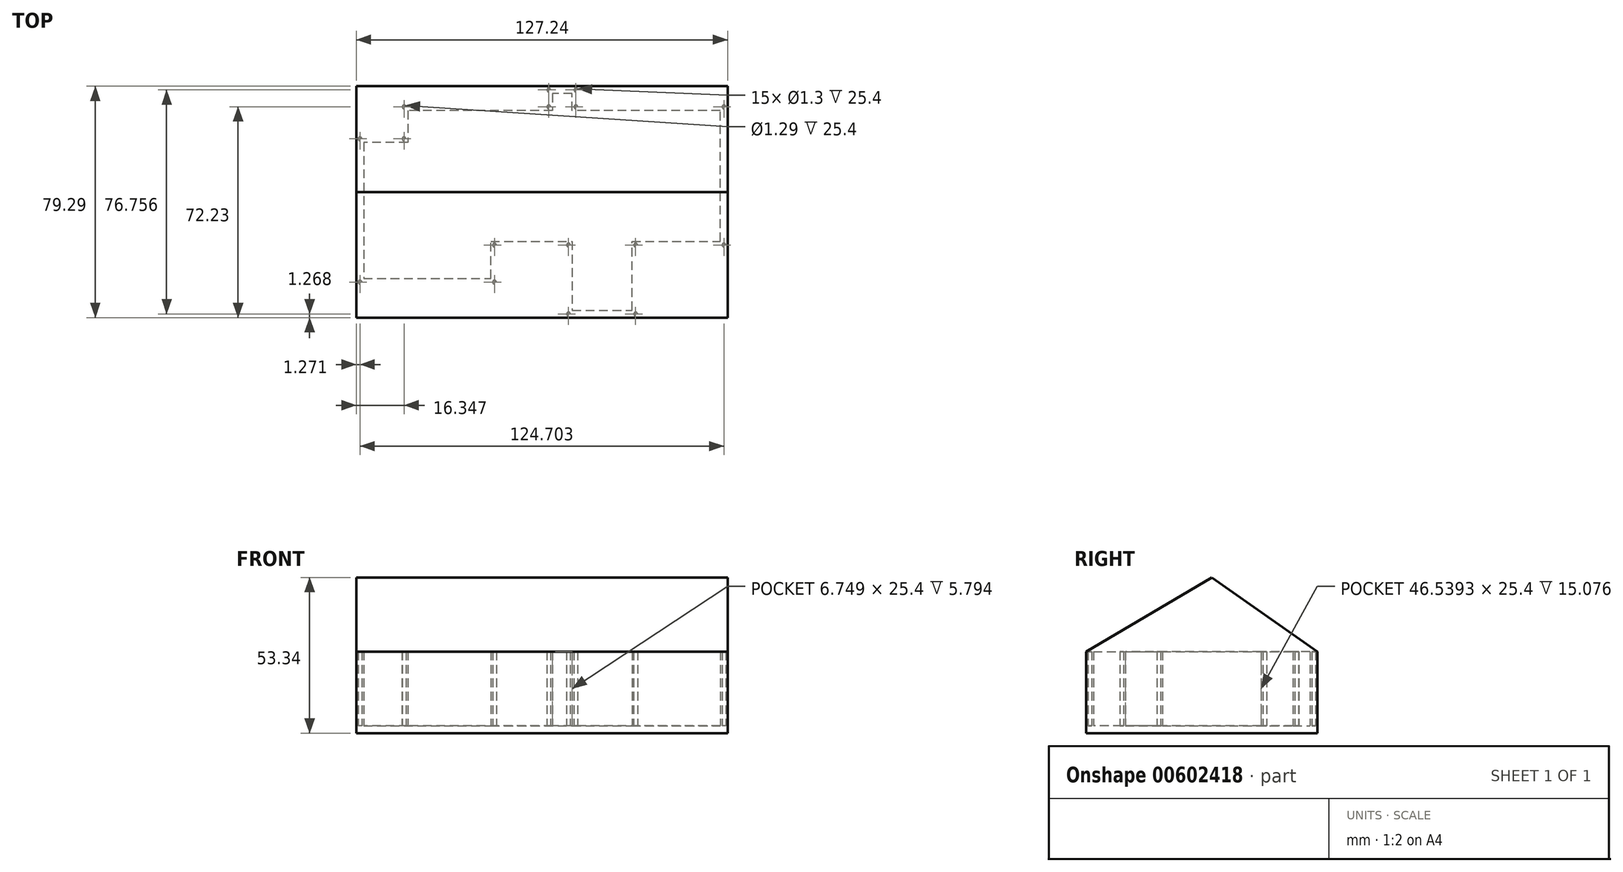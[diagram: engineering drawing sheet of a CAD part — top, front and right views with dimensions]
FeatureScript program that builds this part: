
annotation { "Feature Type Name" : "Feature", "Feature Type Description" : "" }
export const myFeature = defineFeature(function(context is Context, id is Id, definition is map)
    precondition{}
    {
        {
            var Q0;
            Q0=qCreatedBy(makeId("Top.planeOp"),FACE);
            var sketch = newSketch(context, id + "F0", { "sketchPlane" : qUnion([Q0])});
            skLineSegment(sketch, "E0", {"start": v(-47.22, 30.42) * mm, "end": v(2.39, 30.42) * mm});
            skLineSegment(sketch, "E1", {"start": v(2.39, 30.42) * mm, "end": v(2.39, 36.21) * mm});
            skLineSegment(sketch, "E2", {"start": v(2.39, 36.21) * mm, "end": v(14.22, 36.21) * mm});
            skLineSegment(sketch, "E3", {"start": v(14.22, 36.21) * mm, "end": v(14.22, 30.42) * mm});
            skLineSegment(sketch, "E4", {"start": v(14.22, 30.42) * mm, "end": v(64.94, 30.42) * mm});
            skLineSegment(sketch, "E5", {"start": v(-47.22, 30.42) * mm, "end": v(-47.22, 19.46) * mm});
            skLineSegment(sketch, "E6", {"start": v(-47.22, 19.46) * mm, "end": v(-62.3, 19.46) * mm});
            skLineSegment(sketch, "E7", {"start": v(-62.3, 19.46) * mm, "end": v(-62.3, -32.16) * mm});
            skLineSegment(sketch, "E8", {"start": v(-62.3, -32.16) * mm, "end": v(-13.68, -32.16) * mm});
            skLineSegment(sketch, "E9", {"start": v(-13.68, -32.16) * mm, "end": v(-13.68, -19.46) * mm});
            skLineSegment(sketch, "E10", {"start": v(-13.68, -19.46) * mm, "end": v(9.14, -19.46) * mm});
            skLineSegment(sketch, "E11", {"start": v(9.14, -19.46) * mm, "end": v(9.14, -43.08) * mm});
            skLineSegment(sketch, "E12", {"start": v(9.14, -43.08) * mm, "end": v(34.68, -43.08) * mm});
            skLineSegment(sketch, "E13", {"start": v(34.68, -43.08) * mm, "end": v(34.68, -19.46) * mm});
            skLineSegment(sketch, "E14", {"start": v(34.68, -19.46) * mm, "end": v(64.94, -19.46) * mm});
            skLineSegment(sketch, "E15", {"start": v(64.94, -19.46) * mm, "end": v(64.94, 30.42) * mm});
            skLineSegment(sketch, "E16", {"start": v(11.68, -19.46) * mm, "end": v(11.68, -40.54) * mm});
            skLineSegment(sketch, "E17", {"start": v(11.68, -40.54) * mm, "end": v(32.14, -40.54) * mm});
            skLineSegment(sketch, "E18", {"start": v(32.14, -40.54) * mm, "end": v(32.14, -16.92) * mm});
            skLineSegment(sketch, "E19", {"start": v(32.14, -16.92) * mm, "end": v(62.4, -16.92) * mm});
            skLineSegment(sketch, "E20", {"start": v(62.4, -16.92) * mm, "end": v(62.4, 27.88) * mm});
            skLineSegment(sketch, "E21", {"start": v(62.4, 27.88) * mm, "end": v(11.68, 27.88) * mm});
            skLineSegment(sketch, "E22", {"start": v(11.68, 27.88) * mm, "end": v(11.68, 33.67) * mm});
            skLineSegment(sketch, "E23", {"start": v(11.68, 33.67) * mm, "end": v(4.93, 33.67) * mm});
            skLineSegment(sketch, "E24", {"start": v(4.93, 33.67) * mm, "end": v(4.93, 27.88) * mm});
            skLineSegment(sketch, "E25", {"start": v(4.93, 27.88) * mm, "end": v(-44.68, 27.88) * mm});
            skLineSegment(sketch, "E26", {"start": v(-44.68, 27.88) * mm, "end": v(-44.68, 16.92) * mm});
            skLineSegment(sketch, "E27", {"start": v(-44.68, 16.92) * mm, "end": v(-59.76, 16.92) * mm});
            skLineSegment(sketch, "E28", {"start": v(-59.76, 16.92) * mm, "end": v(-59.76, -29.62) * mm});
            skLineSegment(sketch, "E29", {"start": v(-59.76, -29.62) * mm, "end": v(-16.22, -29.62) * mm});
            skLineSegment(sketch, "E30", {"start": v(-16.22, -29.62) * mm, "end": v(-16.22, -16.92) * mm});
            skLineSegment(sketch, "E31", {"start": v(-16.22, -16.92) * mm, "end": v(11.68, -16.92) * mm});
            skLineSegment(sketch, "E32", {"start": v(11.68, -16.92) * mm, "end": v(11.68, -19.46) * mm});
            skLineSegment(sketch, "E33", {"start": v(-59.76, 1.4) * mm, "end": v(62.4, 1.4) * mm});
            skLineSegment(sketch, "E34", {"start": v(-59.76, 2.66) * mm, "end": v(62.4, 2.66) * mm});
            skLineSegment(sketch, "E35", {"start": v(-44.68, 16.92) * mm, "end": v(-44.68, 2.66) * mm});
            skLineSegment(sketch, "E36", {"start": v(-45.95, 16.92) * mm, "end": v(-45.95, 2.66) * mm});
            skLineSegment(sketch, "E37.top", {"start": v(32.14, -43.08) * mm, "end": v(34.68, -43.08) * mm});
            skLineSegment(sketch, "E37.right", {"start": v(34.68, -40.54) * mm, "end": v(34.68, -43.08) * mm});
            skLineSegment(sketch, "E38.top", {"start": v(62.4, 30.42) * mm, "end": v(64.94, 30.42) * mm});
            skLineSegment(sketch, "E38.right", {"start": v(64.94, 27.88) * mm, "end": v(64.94, 30.42) * mm});
            skLineSegment(sketch, "E39.top", {"start": v(-44.68, 30.42) * mm, "end": v(-47.22, 30.42) * mm});
            skLineSegment(sketch, "E39.right", {"start": v(-47.22, 27.88) * mm, "end": v(-47.22, 30.42) * mm});
            skLineSegment(sketch, "E40.bottom", {"start": v(-62.3, -32.16) * mm, "end": v(-59.76, -32.16) * mm});
            skLineSegment(sketch, "E40.left", {"start": v(-62.3, -32.16) * mm, "end": v(-62.3, -29.62) * mm});
            skLineSegment(sketch, "E41.top", {"start": v(-59.76, 19.46) * mm, "end": v(-62.3, 19.46) * mm});
            skLineSegment(sketch, "E41.right", {"start": v(-62.3, 16.92) * mm, "end": v(-62.3, 19.46) * mm});
            skLineSegment(sketch, "E42.top", {"start": v(62.4, -19.46) * mm, "end": v(64.94, -19.46) * mm});
            skLineSegment(sketch, "E42.right", {"start": v(64.94, -16.92) * mm, "end": v(64.94, -19.46) * mm});
            skLineSegment(sketch, "E43.top", {"start": v(34.68, -16.92) * mm, "end": v(32.14, -16.92) * mm});
            skLineSegment(sketch, "E43.right", {"start": v(32.14, -19.46) * mm, "end": v(32.14, -16.92) * mm});
            skLineSegment(sketch, "E44.bottom", {"start": v(9.14, -43.08) * mm, "end": v(11.68, -43.08) * mm});
            skLineSegment(sketch, "E44.left", {"start": v(9.14, -43.08) * mm, "end": v(9.14, -40.54) * mm});
            skLineSegment(sketch, "E45.top", {"start": v(9.14, -16.92) * mm, "end": v(11.68, -16.92) * mm});
            skLineSegment(sketch, "E45.right", {"start": v(11.68, -19.46) * mm, "end": v(11.68, -16.92) * mm});
            skLineSegment(sketch, "E46.top", {"start": v(-13.68, -16.92) * mm, "end": v(-16.22, -16.92) * mm});
            skLineSegment(sketch, "E46.right", {"start": v(-16.22, -19.46) * mm, "end": v(-16.22, -16.92) * mm});
            skLineSegment(sketch, "E47.bottom", {"start": v(14.22, 36.21) * mm, "end": v(11.68, 36.21) * mm});
            skLineSegment(sketch, "E47.left", {"start": v(14.22, 36.21) * mm, "end": v(14.22, 33.67) * mm});
            skLineSegment(sketch, "E48.bottom", {"start": v(2.39, 36.21) * mm, "end": v(4.93, 36.21) * mm});
            skLineSegment(sketch, "E48.left", {"start": v(2.39, 36.21) * mm, "end": v(2.39, 33.67) * mm});
            skLineSegment(sketch, "E49.top", {"start": v(2.39, 27.88) * mm, "end": v(4.93, 27.88) * mm});
            skLineSegment(sketch, "E49.right", {"start": v(4.93, 30.42) * mm, "end": v(4.93, 27.88) * mm});
            skLineSegment(sketch, "E50.bottom", {"start": v(11.68, 27.88) * mm, "end": v(14.22, 27.88) * mm});
            skLineSegment(sketch, "E50.left", {"start": v(11.68, 27.88) * mm, "end": v(11.68, 30.42) * mm});
            skLineSegment(sketch, "E51.bottom", {"start": v(-13.68, -32.16) * mm, "end": v(-16.22, -32.16) * mm});
            skLineSegment(sketch, "E51.left", {"start": v(-13.68, -32.16) * mm, "end": v(-13.68, -29.62) * mm});
            skLineSegment(sketch, "E52.top", {"start": v(-47.22, 16.92) * mm, "end": v(-44.68, 16.92) * mm});
            skLineSegment(sketch, "E52.right", {"start": v(-44.68, 19.46) * mm, "end": v(-44.68, 16.92) * mm});
            skCircle(sketch, "E53", {"center": v(-61.03, 18.2) * mm, "radius": 0.65 * mm});
            skPoint(sketch, "E53.centerSnap0", {"position": v(-62.3, 18.2) * mm});
            skPoint(sketch, "E53.centerSnap1", {"position": v(-61.03, 16.92) * mm});
            skCircle(sketch, "E54", {"center": v(-45.95, 29.15) * mm, "radius": 0.64 * mm});
            skPoint(sketch, "E54.centerSnap0", {"position": v(-45.95, 27.88) * mm});
            skPoint(sketch, "E54.centerSnap1", {"position": v(-47.22, 29.15) * mm});
            skCircle(sketch, "E55", {"center": v(-45.95, 18.2) * mm, "radius": 0.65 * mm});
            skPoint(sketch, "E55.centerSnap0", {"position": v(-47.22, 18.2) * mm});
            skCircle(sketch, "E56", {"center": v(-61.03, -30.89) * mm, "radius": 0.65 * mm});
            skPoint(sketch, "E56.centerSnap0", {"position": v(-61.03, -32.16) * mm});
            skPoint(sketch, "E56.centerSnap1", {"position": v(-59.76, -30.89) * mm});
            skCircle(sketch, "E57", {"center": v(-14.95, -30.89) * mm, "radius": 0.65 * mm});
            skPoint(sketch, "E57.centerSnap0", {"position": v(-14.95, -32.16) * mm});
            skPoint(sketch, "E57.centerSnap1", {"position": v(-13.68, -30.89) * mm});
            skCircle(sketch, "E58", {"center": v(-14.95, -18.19) * mm, "radius": 0.65 * mm});
            skPoint(sketch, "E58.centerSnap0", {"position": v(-16.22, -18.19) * mm});
            skPoint(sketch, "E58.centerSnap1", {"position": v(-14.95, -19.46) * mm});
            skCircle(sketch, "E59", {"center": v(10.4, -18.19) * mm, "radius": 0.65 * mm});
            skPoint(sketch, "E59.centerSnap0", {"position": v(10.4, -19.46) * mm});
            skPoint(sketch, "E59.centerSnap1", {"position": v(11.68, -18.19) * mm});
            skCircle(sketch, "E60", {"center": v(10.4, -41.81) * mm, "radius": 0.65 * mm});
            skPoint(sketch, "E60.centerSnap0", {"position": v(10.4, -43.08) * mm});
            skPoint(sketch, "E60.centerSnap1", {"position": v(9.14, -41.81) * mm});
            skCircle(sketch, "E61", {"center": v(33.41, -41.81) * mm, "radius": 0.65 * mm});
            skPoint(sketch, "E61.centerSnap0", {"position": v(33.41, -43.08) * mm});
            skPoint(sketch, "E61.centerSnap1", {"position": v(32.14, -41.81) * mm});
            skCircle(sketch, "E62", {"center": v(33.41, -18.19) * mm, "radius": 0.65 * mm});
            skPoint(sketch, "E62.centerSnap0", {"position": v(33.41, -19.46) * mm});
            skPoint(sketch, "E62.centerSnap1", {"position": v(32.14, -18.19) * mm});
            skCircle(sketch, "E63", {"center": v(63.67, -18.19) * mm, "radius": 0.65 * mm});
            skPoint(sketch, "E63.centerSnap0", {"position": v(62.4, -18.19) * mm});
            skPoint(sketch, "E63.centerSnap1", {"position": v(63.67, -19.46) * mm});
            skCircle(sketch, "E64", {"center": v(63.67, 29.15) * mm, "radius": 0.65 * mm});
            skPoint(sketch, "E64.centerSnap0", {"position": v(63.67, 27.88) * mm});
            skPoint(sketch, "E64.centerSnap1", {"position": v(64.94, 29.15) * mm});
            skCircle(sketch, "E65", {"center": v(12.95, 29.15) * mm, "radius": 0.65 * mm});
            skPoint(sketch, "E65.centerSnap0", {"position": v(12.95, 27.88) * mm});
            skPoint(sketch, "E65.centerSnap1", {"position": v(14.22, 29.15) * mm});
            skCircle(sketch, "E66", {"center": v(12.95, 34.94) * mm, "radius": 0.65 * mm});
            skPoint(sketch, "E66.centerSnap0", {"position": v(14.22, 34.94) * mm});
            skPoint(sketch, "E66.centerSnap1", {"position": v(12.95, 33.67) * mm});
            skCircle(sketch, "E67", {"center": v(3.66, 34.94) * mm, "radius": 0.65 * mm});
            skPoint(sketch, "E67.centerSnap0", {"position": v(4.93, 34.94) * mm});
            skPoint(sketch, "E67.centerSnap1", {"position": v(3.66, 33.67) * mm});
            skCircle(sketch, "E68", {"center": v(3.66, 29.15) * mm, "radius": 0.65 * mm});
            skPoint(sketch, "E68.centerSnap0", {"position": v(4.93, 29.15) * mm});
            skPoint(sketch, "E68.centerSnap1", {"position": v(3.66, 27.88) * mm});
            skLineSegment(sketch, "E69.bottom", {"start": v(64.94, -19.46) * mm, "end": v(62.4, -19.46) * mm});
            skLineSegment(sketch, "E69.top", {"start": v(64.94, 30.42) * mm, "end": v(62.4, 30.42) * mm});
            skLineSegment(sketch, "E69.right", {"start": v(62.4, -19.46) * mm, "end": v(62.4, 30.42) * mm});
            skLineSegment(sketch, "E70", {"start": v(2.39, 36.21) * mm, "end": v(-62.3, 36.21) * mm});
            skLineSegment(sketch, "E71", {"start": v(-62.3, 36.21) * mm, "end": v(-62.3, 19.46) * mm});
            skLineSegment(sketch, "E72", {"start": v(14.22, 36.21) * mm, "end": v(64.94, 36.21) * mm});
            skLineSegment(sketch, "E73", {"start": v(64.94, 36.21) * mm, "end": v(64.94, 30.42) * mm});
            skLineSegment(sketch, "E74", {"start": v(64.94, -19.46) * mm, "end": v(64.94, -43.08) * mm});
            skLineSegment(sketch, "E75", {"start": v(64.94, -43.08) * mm, "end": v(34.68, -43.08) * mm});
            skLineSegment(sketch, "E76", {"start": v(9.14, -43.08) * mm, "end": v(-62.3, -43.08) * mm});
            skLineSegment(sketch, "E77", {"start": v(-62.3, -43.08) * mm, "end": v(-62.3, -32.16) * mm});
            skSolve(sketch);
        }
        {
            var Q0;
            Q0 = qSketchRegion(id + "F0", true);
            extrude(context, id + "F1", {"entities" : qUnion([Q0]), "depth" : 25.4 * mm, "offsetDistance" : 25.4 * mm});
        }
        {
            var Q0;
            Q0=makeQuery(id+"F1.opExtrude","CAP_FACE",FACE,{"disambiguationData":[OSD([sQuery(id+"F0.wireOp",EDGE,"E2"),sQuery(id+"F0.wireOp",EDGE,"E7"),sQuery(id+"F0.wireOp",EDGE,"E12"),sQuery(id+"F0.wireOp",EDGE,"E16"),sQuery(id+"F0.wireOp",EDGE,"E17"),sQuery(id+"F0.wireOp",EDGE,"E18"),sQuery(id+"F0.wireOp",EDGE,"E19"),sQuery(id+"F0.wireOp",EDGE,"E21"),sQuery(id+"F0.wireOp",EDGE,"E22"),sQuery(id+"F0.wireOp",EDGE,"E23"),sQuery(id+"F0.wireOp",EDGE,"E24"),sQuery(id+"F0.wireOp",EDGE,"E25"),sQuery(id+"F0.wireOp",EDGE,"E26"),sQuery(id+"F0.wireOp",EDGE,"E27"),sQuery(id+"F0.wireOp",EDGE,"E28"),sQuery(id+"F0.wireOp",EDGE,"E29"),sQuery(id+"F0.wireOp",EDGE,"E30"),sQuery(id+"F0.wireOp",EDGE,"E31"),sQuery(id+"F0.wireOp",EDGE,"E37.top"),sQuery(id+"F0.wireOp",EDGE,"E40.left"),sQuery(id+"F0.wireOp",EDGE,"E41.right"),sQuery(id+"F0.wireOp",EDGE,"E43.top"),sQuery(id+"F0.wireOp",EDGE,"E43.right"),sQuery(id+"F0.wireOp",EDGE,"E44.bottom"),sQuery(id+"F0.wireOp",EDGE,"E45.top"),sQuery(id+"F0.wireOp",EDGE,"E45.right"),sQuery(id+"F0.wireOp",EDGE,"E46.top"),sQuery(id+"F0.wireOp",EDGE,"E46.right"),sQuery(id+"F0.wireOp",EDGE,"E47.bottom"),sQuery(id+"F0.wireOp",EDGE,"E48.bottom"),sQuery(id+"F0.wireOp",EDGE,"E49.top"),sQuery(id+"F0.wireOp",EDGE,"E49.right"),sQuery(id+"F0.wireOp",EDGE,"E50.bottom"),sQuery(id+"F0.wireOp",EDGE,"E50.left"),sQuery(id+"F0.wireOp",EDGE,"E52.top"),sQuery(id+"F0.wireOp",EDGE,"E52.right"),sQuery(id+"F0.wireOp",EDGE,"E53"),sQuery(id+"F0.wireOp",EDGE,"E54"),sQuery(id+"F0.wireOp",EDGE,"E55"),sQuery(id+"F0.wireOp",EDGE,"E56"),sQuery(id+"F0.wireOp",EDGE,"E57"),sQuery(id+"F0.wireOp",EDGE,"E58"),sQuery(id+"F0.wireOp",EDGE,"E59"),sQuery(id+"F0.wireOp",EDGE,"E60"),sQuery(id+"F0.wireOp",EDGE,"E61"),sQuery(id+"F0.wireOp",EDGE,"E62"),sQuery(id+"F0.wireOp",EDGE,"E63"),sQuery(id+"F0.wireOp",EDGE,"E64"),sQuery(id+"F0.wireOp",EDGE,"E65"),sQuery(id+"F0.wireOp",EDGE,"E66"),sQuery(id+"F0.wireOp",EDGE,"E67"),sQuery(id+"F0.wireOp",EDGE,"E68"),sQuery(id+"F0.wireOp",EDGE,"E15"),sQuery(id+"F0.wireOp",EDGE,"E69.right"),sQuery(id+"F0.wireOp",EDGE,"E70"),sQuery(id+"F0.wireOp",EDGE,"E71"),sQuery(id+"F0.wireOp",EDGE,"E72"),sQuery(id+"F0.wireOp",EDGE,"E73"),sQuery(id+"F0.wireOp",EDGE,"E74"),sQuery(id+"F0.wireOp",EDGE,"E75"),sQuery(id+"F0.wireOp",EDGE,"E76"),sQuery(id+"F0.wireOp",EDGE,"E77")])],"isStart":false});
            var sketch = newSketch(context, id + "F2", { "sketchPlane" : qUnion([Q0])});
            skLineSegment(sketch, "E78", {"start": v(-62.3, 0) * mm, "end": v(64.94, 0) * mm});
            skLineSegment(sketch, "E79", {"start": v(-62.3, 0) * mm, "end": v(-62.3, -43.08) * mm});
            skLineSegment(sketch, "E80", {"start": v(-62.3, -43.08) * mm, "end": v(64.94, -43.08) * mm});
            skLineSegment(sketch, "E81", {"start": v(64.94, -43.08) * mm, "end": v(64.94, 0) * mm});
            skSolve(sketch);
        }
        {
            var Q0;
            Q0 = qSketchRegion(id + "F2", true);
            extrude(context, id + "F3", {"entities" : qUnion([Q0]), "operationType" : NewBodyOperationType.ADD, "depth" : 25.4 * mm, "offsetDistance" : 25.4 * mm});
        }
        {
            var Q0;
            Q0=makeQuery(id+"F3.boolean.opBoolean","MERGE",FACE,{"derivedFrom":[makeQuery(id+"F1.opExtrude","SWEPT_FACE",FACE,{"disambiguationData":[OSD([sQuery(id+"F0.wireOp",EDGE,"E15"),sQuery(id+"F0.wireOp",EDGE,"E73"),sQuery(id+"F0.wireOp",EDGE,"E74")])]}),makeQuery(id+"F3.opExtrude","SWEPT_FACE",FACE,{"disambiguationData":[OSD([sQuery(id+"F2.wireOp",EDGE,"E81")])]})]});
            var sketch = newSketch(context, id + "F4", { "sketchPlane" : qUnion([Q0])});
            skLineSegment(sketch, "E82", {"start": v(0, 25.4) * mm, "end": v(-43.08, 25.4) * mm});
            skSolve(sketch);
        }
        {
            var Q0;
            {var subQ0=sQuery(id+"F4.wireOp",EDGE,"E82");Q0=makeQuery(id+"F4.imprint","IMPRINT",FACE,{"disambiguationData":[TD([[makeQuery(id+"F4.imprint","IMPRINT",EDGE,{"derivedFrom":subQ0}),-1.0]])]});}
            var sketch = newSketch(context, id + "F5", { "sketchPlane" : qUnion([Q0])});
            skLineSegment(sketch, "E83", {"start": v(-43.08, 25.4) * mm, "end": v(0, 50.8) * mm});
            skSolve(sketch);
        }
        {
            var Q0;
            {var subQ0=sQuery(id+"F5.wireOp",EDGE,"E83");Q0=makeQuery(id+"F5.imprint","IMPRINT",FACE,{"disambiguationData":[TD([[makeQuery(id+"F5.imprint","IMPRINT",EDGE,{"derivedFrom":subQ0}),1.0]])]});}
            extrude(context, id + "F6", {"entities" : qUnion([Q0]), "operationType" : NewBodyOperationType.REMOVE, "endBound" : BoundingType.THROUGH_ALL, "oppositeDirection" : true, "depth" : 25.4 * mm, "offsetDistance" : 25.4 * mm});
        }
        {
            var Q0;
            Q0=makeQuery(id+"F1.opExtrude","CAP_FACE",FACE,{"disambiguationData":[OSD([sQuery(id+"F0.wireOp",EDGE,"E2"),sQuery(id+"F0.wireOp",EDGE,"E7"),sQuery(id+"F0.wireOp",EDGE,"E12"),sQuery(id+"F0.wireOp",EDGE,"E16"),sQuery(id+"F0.wireOp",EDGE,"E17"),sQuery(id+"F0.wireOp",EDGE,"E18"),sQuery(id+"F0.wireOp",EDGE,"E19"),sQuery(id+"F0.wireOp",EDGE,"E21"),sQuery(id+"F0.wireOp",EDGE,"E22"),sQuery(id+"F0.wireOp",EDGE,"E23"),sQuery(id+"F0.wireOp",EDGE,"E24"),sQuery(id+"F0.wireOp",EDGE,"E25"),sQuery(id+"F0.wireOp",EDGE,"E26"),sQuery(id+"F0.wireOp",EDGE,"E27"),sQuery(id+"F0.wireOp",EDGE,"E28"),sQuery(id+"F0.wireOp",EDGE,"E29"),sQuery(id+"F0.wireOp",EDGE,"E30"),sQuery(id+"F0.wireOp",EDGE,"E31"),sQuery(id+"F0.wireOp",EDGE,"E37.top"),sQuery(id+"F0.wireOp",EDGE,"E40.left"),sQuery(id+"F0.wireOp",EDGE,"E41.right"),sQuery(id+"F0.wireOp",EDGE,"E43.top"),sQuery(id+"F0.wireOp",EDGE,"E43.right"),sQuery(id+"F0.wireOp",EDGE,"E44.bottom"),sQuery(id+"F0.wireOp",EDGE,"E45.top"),sQuery(id+"F0.wireOp",EDGE,"E45.right"),sQuery(id+"F0.wireOp",EDGE,"E46.top"),sQuery(id+"F0.wireOp",EDGE,"E46.right"),sQuery(id+"F0.wireOp",EDGE,"E47.bottom"),sQuery(id+"F0.wireOp",EDGE,"E48.bottom"),sQuery(id+"F0.wireOp",EDGE,"E49.top"),sQuery(id+"F0.wireOp",EDGE,"E49.right"),sQuery(id+"F0.wireOp",EDGE,"E50.bottom"),sQuery(id+"F0.wireOp",EDGE,"E50.left"),sQuery(id+"F0.wireOp",EDGE,"E52.top"),sQuery(id+"F0.wireOp",EDGE,"E52.right"),sQuery(id+"F0.wireOp",EDGE,"E53"),sQuery(id+"F0.wireOp",EDGE,"E54"),sQuery(id+"F0.wireOp",EDGE,"E55"),sQuery(id+"F0.wireOp",EDGE,"E56"),sQuery(id+"F0.wireOp",EDGE,"E57"),sQuery(id+"F0.wireOp",EDGE,"E58"),sQuery(id+"F0.wireOp",EDGE,"E59"),sQuery(id+"F0.wireOp",EDGE,"E60"),sQuery(id+"F0.wireOp",EDGE,"E61"),sQuery(id+"F0.wireOp",EDGE,"E62"),sQuery(id+"F0.wireOp",EDGE,"E63"),sQuery(id+"F0.wireOp",EDGE,"E64"),sQuery(id+"F0.wireOp",EDGE,"E65"),sQuery(id+"F0.wireOp",EDGE,"E66"),sQuery(id+"F0.wireOp",EDGE,"E67"),sQuery(id+"F0.wireOp",EDGE,"E68"),sQuery(id+"F0.wireOp",EDGE,"E15"),sQuery(id+"F0.wireOp",EDGE,"E69.right"),sQuery(id+"F0.wireOp",EDGE,"E70"),sQuery(id+"F0.wireOp",EDGE,"E71"),sQuery(id+"F0.wireOp",EDGE,"E72"),sQuery(id+"F0.wireOp",EDGE,"E73"),sQuery(id+"F0.wireOp",EDGE,"E74"),sQuery(id+"F0.wireOp",EDGE,"E75"),sQuery(id+"F0.wireOp",EDGE,"E76"),sQuery(id+"F0.wireOp",EDGE,"E77")])],"isStart":false});
            var sketch = newSketch(context, id + "F7", { "sketchPlane" : qUnion([Q0])});
            skLineSegment(sketch, "E84", {"start": v(64.94, 0) * mm, "end": v(64.94, 36.21) * mm});
            skLineSegment(sketch, "E85", {"start": v(64.94, 36.21) * mm, "end": v(-62.3, 36.21) * mm});
            skLineSegment(sketch, "E86", {"start": v(-62.3, 36.21) * mm, "end": v(-62.3, 0) * mm});
            skLineSegment(sketch, "E87", {"start": v(-62.3, 0) * mm, "end": v(64.94, 0) * mm});
            skSolve(sketch);
        }
        {
            var Q0;
            Q0 = qSketchRegion(id + "F7", true);
            extrude(context, id + "F8", {"entities" : qUnion([Q0]), "operationType" : NewBodyOperationType.ADD, "depth" : 25.4 * mm, "offsetDistance" : 25.4 * mm});
        }
        {
            var Q0;
            Q0=makeQuery(id+"F8.boolean.opBoolean","MERGE",FACE,{"derivedFrom":[makeQuery(id+"F3.boolean.opBoolean","MERGE",FACE,{"derivedFrom":[makeQuery(id+"F1.opExtrude","SWEPT_FACE",FACE,{"disambiguationData":[OSD([sQuery(id+"F0.wireOp",EDGE,"E7"),sQuery(id+"F0.wireOp",EDGE,"E40.left"),sQuery(id+"F0.wireOp",EDGE,"E41.right"),sQuery(id+"F0.wireOp",EDGE,"E71"),sQuery(id+"F0.wireOp",EDGE,"E77")])]}),makeQuery(id+"F3.opExtrude","SWEPT_FACE",FACE,{"disambiguationData":[OSD([sQuery(id+"F2.wireOp",EDGE,"E79")])]})]}),makeQuery(id+"F8.opExtrude","SWEPT_FACE",FACE,{"disambiguationData":[OSD([sQuery(id+"F7.wireOp",EDGE,"E86")])]})]});
            var sketch = newSketch(context, id + "F9", { "sketchPlane" : qUnion([Q0])});
            skLineSegment(sketch, "E88", {"start": v(0, 50.8) * mm, "end": v(-36.21, 25.4) * mm});
            skSolve(sketch);
        }
        {
            var Q0;
            Q0=makeQuery(id+"F8.boolean.opBoolean","MERGE",FACE,{"derivedFrom":[makeQuery(id+"F1.opExtrude","SWEPT_FACE",FACE,{"disambiguationData":[OSD([sQuery(id+"F0.wireOp",EDGE,"E2"),sQuery(id+"F0.wireOp",EDGE,"E47.bottom"),sQuery(id+"F0.wireOp",EDGE,"E48.bottom"),sQuery(id+"F0.wireOp",EDGE,"E70"),sQuery(id+"F0.wireOp",EDGE,"E72")])]}),makeQuery(id+"F8.opExtrude","SWEPT_FACE",FACE,{"disambiguationData":[OSD([sQuery(id+"F7.wireOp",EDGE,"E85")])]})]});
            var sketch = newSketch(context, id + "F10", { "sketchPlane" : qUnion([Q0])});
            skLineSegment(sketch, "E89", {"start": v(62.3, 25.4) * mm, "end": v(-64.94, 25.4) * mm});
            skSolve(sketch);
        }
        {
            var Q0;
            Q0 = qSketchRegion(id + "F10", true);
            var Q1;
            {var subQ0=sQuery(id+"F9.wireOp",EDGE,"E88");Q1=makeQuery(id+"F9.imprint","IMPRINT",FACE,{"disambiguationData":[TD([[makeQuery(id+"F9.imprint","IMPRINT",EDGE,{"derivedFrom":subQ0}),-1.0]])]});}
            extrude(context, id + "F11", {"entities" : qUnion([Q0, Q1]), "operationType" : NewBodyOperationType.REMOVE, "endBound" : BoundingType.THROUGH_ALL, "oppositeDirection" : true, "depth" : 25.4 * mm, "offsetDistance" : 25.4 * mm});
        }
        {
            var Q0;
            Q0=makeQuery(id+"F1.opExtrude","CAP_FACE",FACE,{"disambiguationData":[OSD([sQuery(id+"F0.wireOp",EDGE,"E2"),sQuery(id+"F0.wireOp",EDGE,"E7"),sQuery(id+"F0.wireOp",EDGE,"E12"),sQuery(id+"F0.wireOp",EDGE,"E16"),sQuery(id+"F0.wireOp",EDGE,"E17"),sQuery(id+"F0.wireOp",EDGE,"E18"),sQuery(id+"F0.wireOp",EDGE,"E19"),sQuery(id+"F0.wireOp",EDGE,"E21"),sQuery(id+"F0.wireOp",EDGE,"E22"),sQuery(id+"F0.wireOp",EDGE,"E23"),sQuery(id+"F0.wireOp",EDGE,"E24"),sQuery(id+"F0.wireOp",EDGE,"E25"),sQuery(id+"F0.wireOp",EDGE,"E26"),sQuery(id+"F0.wireOp",EDGE,"E27"),sQuery(id+"F0.wireOp",EDGE,"E28"),sQuery(id+"F0.wireOp",EDGE,"E29"),sQuery(id+"F0.wireOp",EDGE,"E30"),sQuery(id+"F0.wireOp",EDGE,"E31"),sQuery(id+"F0.wireOp",EDGE,"E37.top"),sQuery(id+"F0.wireOp",EDGE,"E40.left"),sQuery(id+"F0.wireOp",EDGE,"E41.right"),sQuery(id+"F0.wireOp",EDGE,"E43.top"),sQuery(id+"F0.wireOp",EDGE,"E43.right"),sQuery(id+"F0.wireOp",EDGE,"E44.bottom"),sQuery(id+"F0.wireOp",EDGE,"E45.top"),sQuery(id+"F0.wireOp",EDGE,"E45.right"),sQuery(id+"F0.wireOp",EDGE,"E46.top"),sQuery(id+"F0.wireOp",EDGE,"E46.right"),sQuery(id+"F0.wireOp",EDGE,"E47.bottom"),sQuery(id+"F0.wireOp",EDGE,"E48.bottom"),sQuery(id+"F0.wireOp",EDGE,"E49.top"),sQuery(id+"F0.wireOp",EDGE,"E49.right"),sQuery(id+"F0.wireOp",EDGE,"E50.bottom"),sQuery(id+"F0.wireOp",EDGE,"E50.left"),sQuery(id+"F0.wireOp",EDGE,"E52.top"),sQuery(id+"F0.wireOp",EDGE,"E52.right"),sQuery(id+"F0.wireOp",EDGE,"E53"),sQuery(id+"F0.wireOp",EDGE,"E54"),sQuery(id+"F0.wireOp",EDGE,"E55"),sQuery(id+"F0.wireOp",EDGE,"E56"),sQuery(id+"F0.wireOp",EDGE,"E57"),sQuery(id+"F0.wireOp",EDGE,"E58"),sQuery(id+"F0.wireOp",EDGE,"E59"),sQuery(id+"F0.wireOp",EDGE,"E60"),sQuery(id+"F0.wireOp",EDGE,"E61"),sQuery(id+"F0.wireOp",EDGE,"E62"),sQuery(id+"F0.wireOp",EDGE,"E63"),sQuery(id+"F0.wireOp",EDGE,"E64"),sQuery(id+"F0.wireOp",EDGE,"E65"),sQuery(id+"F0.wireOp",EDGE,"E66"),sQuery(id+"F0.wireOp",EDGE,"E67"),sQuery(id+"F0.wireOp",EDGE,"E68"),sQuery(id+"F0.wireOp",EDGE,"E15"),sQuery(id+"F0.wireOp",EDGE,"E69.right"),sQuery(id+"F0.wireOp",EDGE,"E70"),sQuery(id+"F0.wireOp",EDGE,"E71"),sQuery(id+"F0.wireOp",EDGE,"E72"),sQuery(id+"F0.wireOp",EDGE,"E73"),sQuery(id+"F0.wireOp",EDGE,"E74"),sQuery(id+"F0.wireOp",EDGE,"E75"),sQuery(id+"F0.wireOp",EDGE,"E76"),sQuery(id+"F0.wireOp",EDGE,"E77")])],"isStart":true});
            var sketch = newSketch(context, id + "F12", { "sketchPlane" : qUnion([Q0])});
            skLineSegment(sketch, "E90.0", {"start": v(64.94, -36.21) * mm, "end": v(-62.3, -36.21) * mm});
            skLineSegment(sketch, "E91.0", {"start": v(64.94, -36.21) * mm, "end": v(64.94, 43.08) * mm});
            skLineSegment(sketch, "E92.0", {"start": v(64.94, 43.08) * mm, "end": v(-62.3, 43.08) * mm});
            skLineSegment(sketch, "E93.0", {"start": v(-62.3, -36.21) * mm, "end": v(-62.3, 43.08) * mm});
            skSolve(sketch);
        }
        {
            var Q0;
            Q0 = qSketchRegion(id + "F12", true);
            extrude(context, id + "F13", {"entities" : qUnion([Q0]), "operationType" : NewBodyOperationType.ADD, "depth" : 2.54 * mm, "offsetDistance" : 25.4 * mm});
        }
    });
